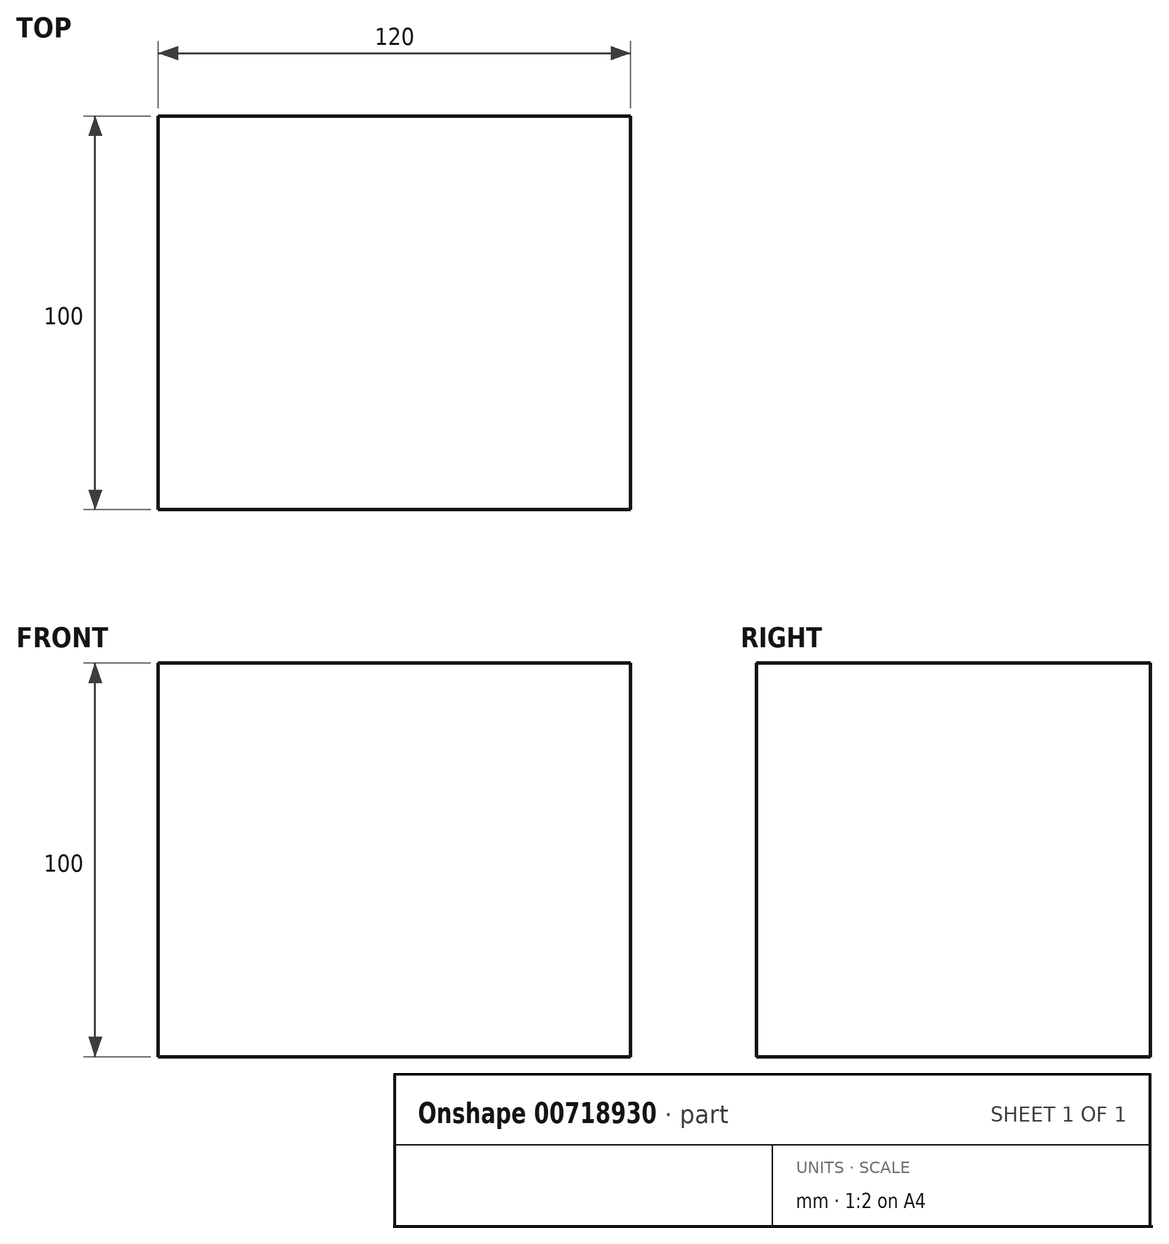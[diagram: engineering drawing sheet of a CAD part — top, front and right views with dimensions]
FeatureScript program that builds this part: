
annotation { "Feature Type Name" : "Feature", "Feature Type Description" : "" }
export const myFeature = defineFeature(function(context is Context, id is Id, definition is map)
    precondition{}
    {
        {
            var Q0;
            Q0=qCreatedBy(makeId("Top.planeOp"),FACE);
            var sketch = newSketch(context, id + "F0", { "sketchPlane" : qUnion([Q0])});
            skLineSegment(sketch, "E0.bottom", {"start": v(0, 100) * mm, "end": v(-120, 100) * mm});
            skLineSegment(sketch, "E0.top", {"start": v(0, 0) * mm, "end": v(-120, 0) * mm});
            skLineSegment(sketch, "E0.left", {"start": v(0, 100) * mm, "end": v(0, 0) * mm});
            skLineSegment(sketch, "E0.right", {"start": v(-120, 100) * mm, "end": v(-120, 0) * mm});
            skSolve(sketch);
        }
        {
            var Q0;
            Q0 = qSketchRegion(id + "F0", true);
            extrude(context, id + "F1", {"entities" : qUnion([Q0]), "depth" : 100 * mm, "offsetDistance" : 25 * mm});
        }
    });
